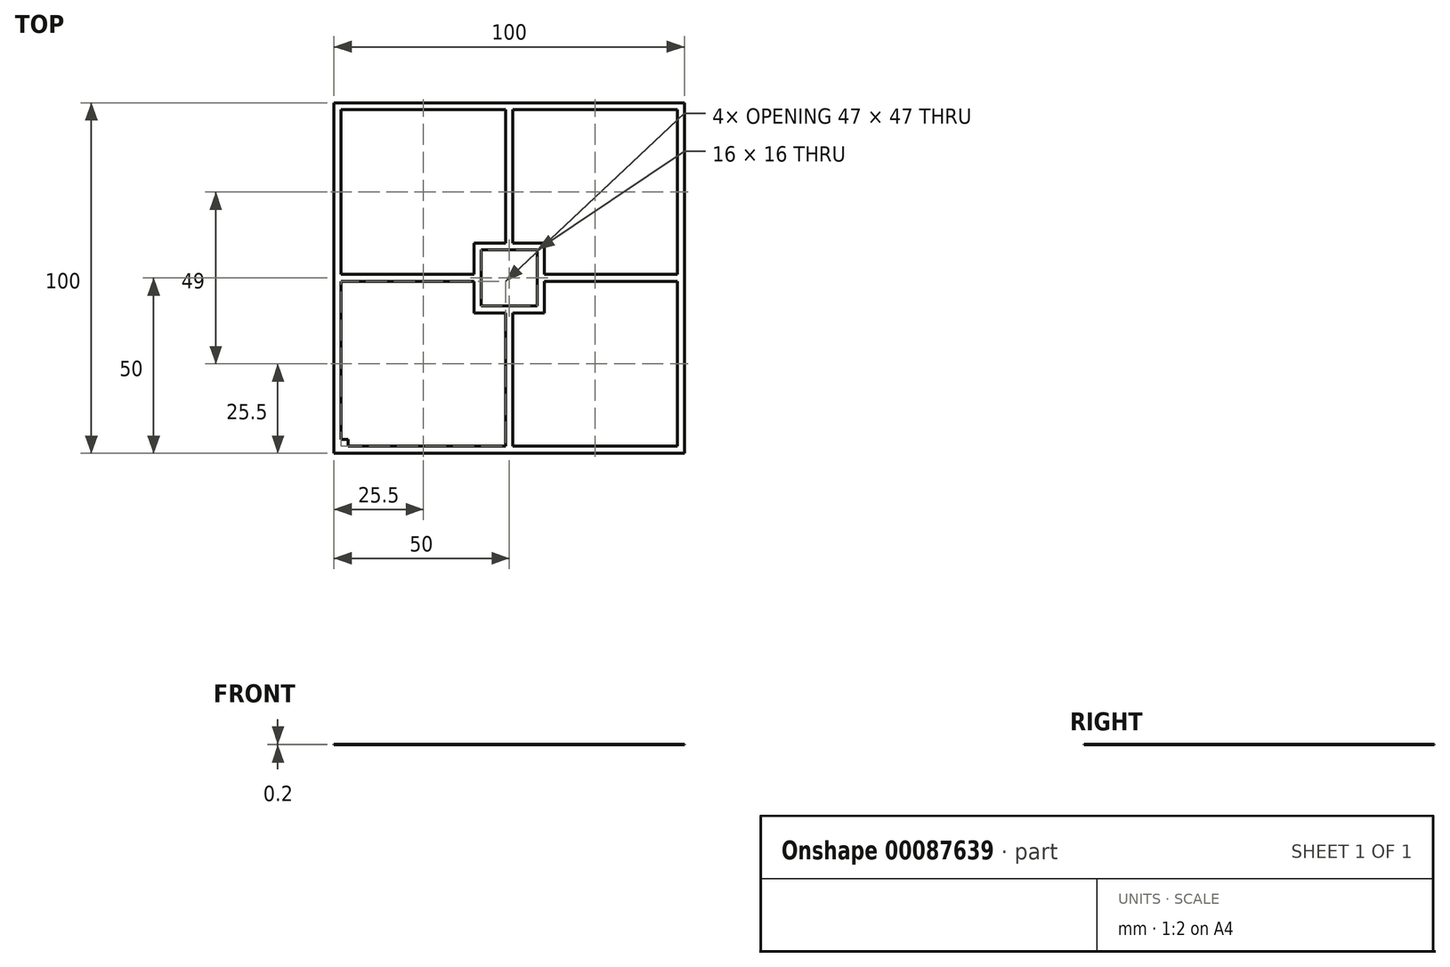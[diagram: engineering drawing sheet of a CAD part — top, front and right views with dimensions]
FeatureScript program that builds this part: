
annotation { "Feature Type Name" : "Feature", "Feature Type Description" : "" }
export const myFeature = defineFeature(function(context is Context, id is Id, definition is map)
    precondition{}
    {
        {
            var Q0;
            Q0=qCreatedBy(makeId("Top.planeOp"),FACE);
            var sketch = newSketch(context, id + "F0", { "sketchPlane" : qUnion([Q0])});
            skLineSegment(sketch, "E0.bottom", {"start": v(50, 50) * mm, "end": v(-50, 50) * mm});
            skLineSegment(sketch, "E0.top", {"start": v(50, -50) * mm, "end": v(-50, -50) * mm});
            skLineSegment(sketch, "E0.left", {"start": v(50, 50) * mm, "end": v(50, -50) * mm});
            skLineSegment(sketch, "E0.right", {"start": v(-50, 50) * mm, "end": v(-50, -50) * mm});
            skLineSegment(sketch, "E1.0", {"start": v(48, 48) * mm, "end": v(1, 48) * mm});
            skLineSegment(sketch, "E1.1", {"start": v(48, 48) * mm, "end": v(48, 1) * mm});
            skLineSegment(sketch, "E1.2", {"start": v(48, -48) * mm, "end": v(-46, -48) * mm});
            skLineSegment(sketch, "E1.3", {"start": v(-48, 48) * mm, "end": v(-48, 1) * mm});
            skLineSegment(sketch, "E2.bottom", {"start": v(10, -10) * mm, "end": v(1, -10) * mm});
            skLineSegment(sketch, "E2.top", {"start": v(10, 10) * mm, "end": v(1, 10) * mm});
            skLineSegment(sketch, "E2.left", {"start": v(10, -10) * mm, "end": v(10, -1) * mm});
            skLineSegment(sketch, "E2.right", {"start": v(-10, -10) * mm, "end": v(-10, -1) * mm});
            skLineSegment(sketch, "E3", {"start": v(-10, 1) * mm, "end": v(-48, 1) * mm});
            skLineSegment(sketch, "E4", {"start": v(-10, -1) * mm, "end": v(-48, -1) * mm});
            skLineSegment(sketch, "E5", {"start": v(-1, 10) * mm, "end": v(-1, 48) * mm});
            skLineSegment(sketch, "E6", {"start": v(1, 10) * mm, "end": v(1, 48) * mm});
            skLineSegment(sketch, "E7", {"start": v(1, 48) * mm, "end": v(20.1, 32.82) * mm});
            skLineSegment(sketch, "E8", {"start": v(10, 1) * mm, "end": v(48, 1) * mm});
            skLineSegment(sketch, "E9", {"start": v(10, -1) * mm, "end": v(48, -1) * mm});
            skLineSegment(sketch, "E10", {"start": v(1, -10) * mm, "end": v(1, -48) * mm});
            skLineSegment(sketch, "E11", {"start": v(-1, -10) * mm, "end": v(-1, -48) * mm});
            skLineSegment(sketch, "E12.trimOffspring", {"start": v(-10, 1) * mm, "end": v(-10, 10) * mm});
            skLineSegment(sketch, "E13.trimOffspring", {"start": v(10, 1) * mm, "end": v(10, 10) * mm});
            skLineSegment(sketch, "E14.trimOffspring", {"start": v(-1, 10) * mm, "end": v(-10, 10) * mm});
            skLineSegment(sketch, "E15.trimOffspring", {"start": v(-1, 48) * mm, "end": v(-48, 48) * mm});
            skLineSegment(sketch, "E16.trimOffspring", {"start": v(48, -1) * mm, "end": v(48, -48) * mm});
            skLineSegment(sketch, "E17.trimOffspring", {"start": v(-48, -1) * mm, "end": v(-48, -46) * mm});
            skLineSegment(sketch, "E18.trimOffspring", {"start": v(-1, -10) * mm, "end": v(-10, -10) * mm});
            skLineSegment(sketch, "E19.bottom", {"start": v(-50, -50) * mm, "end": v(-46, -50) * mm});
            skLineSegment(sketch, "E19.top", {"start": v(-48, -46) * mm, "end": v(-46, -46) * mm});
            skLineSegment(sketch, "E19.left", {"start": v(-50, -50) * mm, "end": v(-50, -46) * mm});
            skLineSegment(sketch, "E19.right", {"start": v(-46, -48) * mm, "end": v(-46, -46) * mm});
            skPoint(sketch, "E19.middle", {"position": v(-48, -48) * mm});
            skLineSegment(sketch, "E20.0", {"start": v(-8, 1) * mm, "end": v(-8, 8) * mm});
            skLineSegment(sketch, "E20.1", {"start": v(-1, 8) * mm, "end": v(-8, 8) * mm});
            skLineSegment(sketch, "E21.0", {"start": v(8, -8) * mm, "end": v(8, -1) * mm});
            skLineSegment(sketch, "E21.1", {"start": v(8, -8) * mm, "end": v(1, -8) * mm});
            skLineSegment(sketch, "E22.bottom", {"start": v(-8, 8) * mm, "end": v(8, 8) * mm});
            skLineSegment(sketch, "E22.top", {"start": v(-8, -8) * mm, "end": v(8, -8) * mm});
            skLineSegment(sketch, "E22.left", {"start": v(-8, 8) * mm, "end": v(-8, -8) * mm});
            skLineSegment(sketch, "E22.right", {"start": v(8, 8) * mm, "end": v(8, -8) * mm});
            skSolve(sketch);
        }
        {
            var Q0;
            Q0=makeQuery(id+"F0.imprint","IMPRINT",FACE,{"disambiguationData":[TD([[makeQuery(id+"F0.imprint","IMPRINT",EDGE,{"derivedFrom":sQuery(id+"F0.wireOp",EDGE,"E0.bottom")}),1.0]])]});
            extrude(context, id + "F1", {"entities" : qUnion([Q0]), "depth" : 0.2 * mm});
        }
    });
